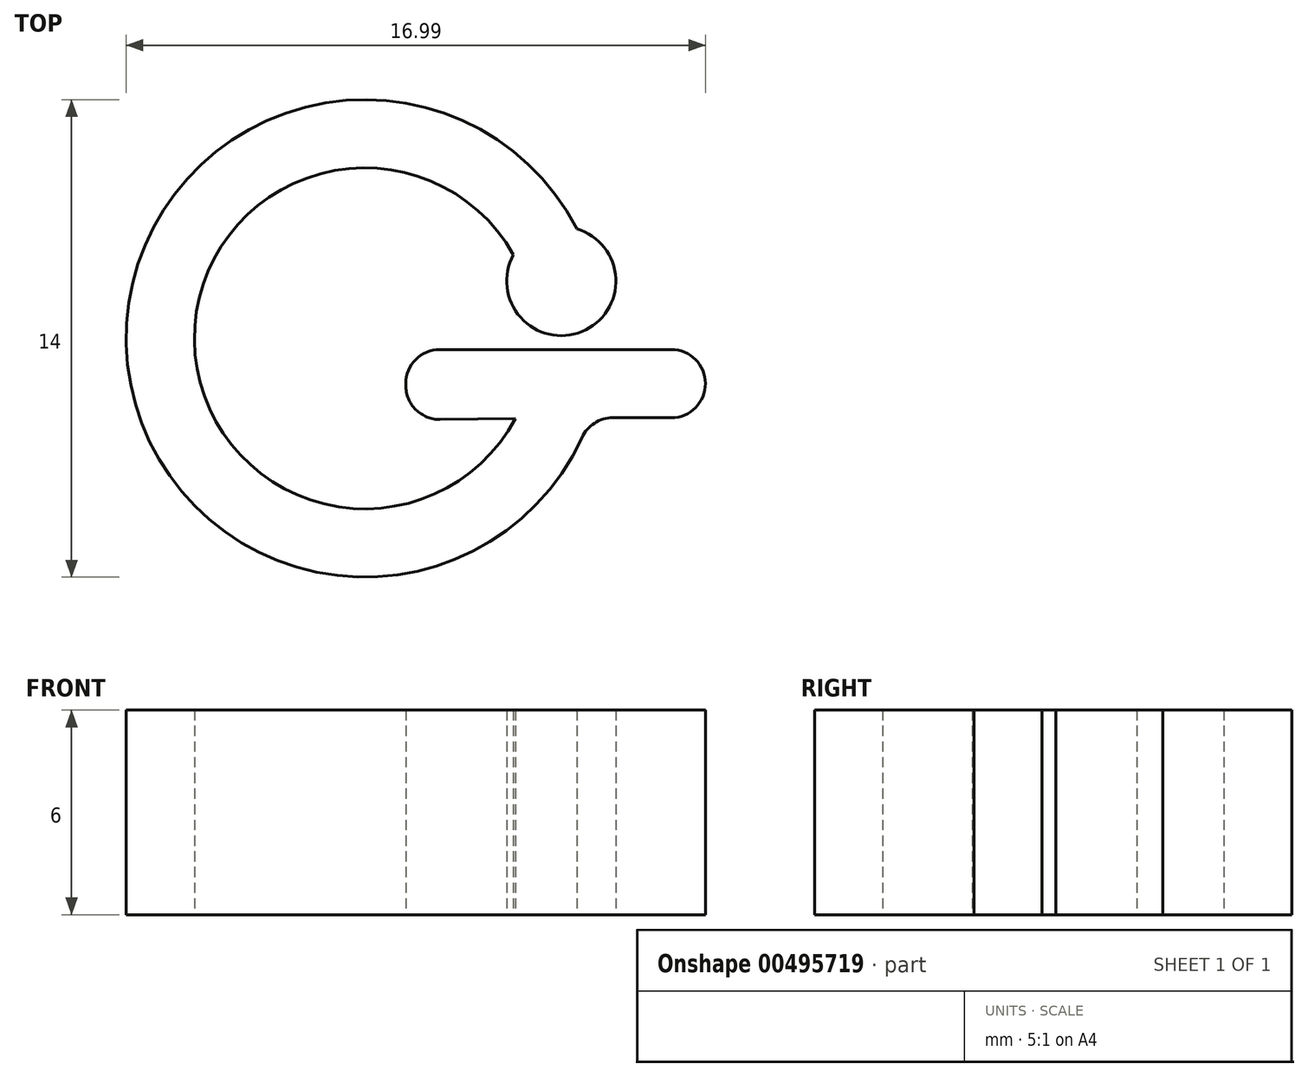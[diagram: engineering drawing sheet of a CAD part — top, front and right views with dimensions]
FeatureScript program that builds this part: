
annotation { "Feature Type Name" : "Feature", "Feature Type Description" : "" }
export const myFeature = defineFeature(function(context is Context, id is Id, definition is map)
    precondition{}
    {
        {
            var Q0;
            Q0=qCreatedBy(makeId("Top.planeOp"),FACE);
            var sketch = newSketch(context, id + "F0", { "sketchPlane" : qUnion([Q0]), "disableImprinting" : false});
            skArc(sketch, "E0", {"start": v(4.36, 2.45) * mm, "mid": v(-5, -0.06) * mm, "end": v(4.41, -2.35) * mm});
            skArc(sketch, "E1", {"start": v(6.22, 3.21) * mm, "mid": v(-6.98, -0.48) * mm, "end": v(6.6, -2.33) * mm});
            skCircle(sketch, "E2", {"center": v(0, 0) * mm, "radius": 6 * mm, "construction": true});
            skLineSegment(sketch, "E3", {"start": v(0, 0) * mm, "end": v(9.75, 0) * mm, "construction": true});
            skArc(sketch, "E4", {"start": v(4.36, 2.45) * mm, "mid": v(6.37, 0.2) * mm, "end": v(6.22, 3.21) * mm});
            skLineSegment(sketch, "E5", {"start": v(4.99, -0.33) * mm, "end": v(9.99, -0.33) * mm});
            skLineSegment(sketch, "E6", {"start": v(9.99, -0.33) * mm, "end": v(9.99, -2.33) * mm});
            skLineSegment(sketch, "E7", {"start": v(9.99, -2.33) * mm, "end": v(6.6, -2.33) * mm});
            skLineSegment(sketch, "E8", {"start": v(4.99, -0.33) * mm, "end": v(1.2, -0.33) * mm});
            skLineSegment(sketch, "E9", {"start": v(1.2, -0.33) * mm, "end": v(1.2, -2.4) * mm});
            skLineSegment(sketch, "E10", {"start": v(1.2, -2.4) * mm, "end": v(4.41, -2.35) * mm});
            skSolve(sketch);
        }
        {
            var Q0;
            Q0=makeQuery(id+"F0.imprint","IMPRINT",FACE,{"disambiguationData":[TD([[makeQuery(id+"F0.imprint","IMPRINT",EDGE,{"derivedFrom":sQuery(id+"F0.wireOp",EDGE,"E0")}),-1.0]])]});
            extrude(context, id + "F1", {"entities" : qUnion([Q0]), "depth" : 6 * mm, "offsetDistance" : 25 * mm});
        }
        {
            var Q0;
            Q0=makeQuery(id+"F1.opExtrude","SWEPT_EDGE",EDGE,{"disambiguationData":[OSD([sQuery(id+"F0.wireOp",EDGE,"E5"),sQuery(id+"F0.wireOp",EDGE,"E6")])]});
            var Q1;
            Q1=makeQuery(id+"F1.opExtrude","SWEPT_EDGE",EDGE,{"disambiguationData":[OSD([sQuery(id+"F0.wireOp",EDGE,"E8"),sQuery(id+"F0.wireOp",EDGE,"E9")])]});
            var Q2;
            Q2=makeQuery(id+"F1.opExtrude","SWEPT_EDGE",EDGE,{"disambiguationData":[OSD([sQuery(id+"F0.wireOp",EDGE,"E9"),sQuery(id+"F0.wireOp",EDGE,"E10")])]});
            var Q3;
            Q3=makeQuery(id+"F1.opExtrude","SWEPT_EDGE",EDGE,{"disambiguationData":[OSD([sQuery(id+"F0.wireOp",EDGE,"E6"),sQuery(id+"F0.wireOp",EDGE,"E7")])]});
            var Q4;
            Q4=makeQuery(id+"F1.opExtrude","SWEPT_EDGE",EDGE,{"disambiguationData":[OSD([sQuery(id+"F0.wireOp",EDGE,"E1"),sQuery(id+"F0.wireOp",EDGE,"E7")])]});
            fillet(context, id + "F2", {"entities" : qUnion([Q0, Q1, Q2, Q3, Q4]), "radius" : 1 * mm, "tangentPropagation" : true, "allowEdgeOverflow" : false});
        }
    });
